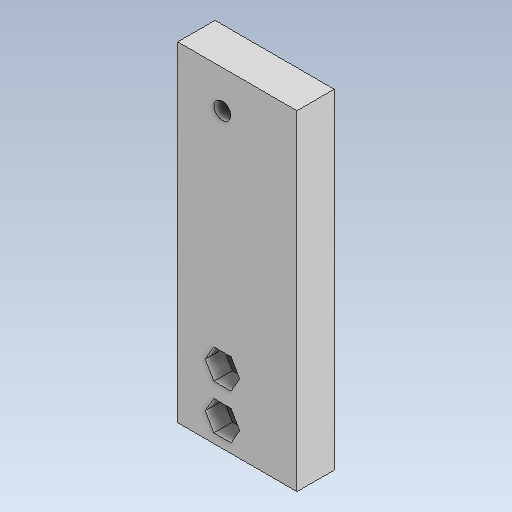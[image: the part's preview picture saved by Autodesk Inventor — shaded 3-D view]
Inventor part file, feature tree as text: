
AUTODESK INVENTOR PART (.ipt)
format: ipt  version: 2020 (Build 240168000, 168)  size: 152,576 bytes
history: native  units: mm
features: other x11, reference x8, sketch x5, extrude x3, projected_geometry x3, hole x2
ambient origin geometry x8: Origin, YZ Plane, XZ Plane, XY Plane, X Axis, Y Axis, Z Axis, Center Point
bodies: Body1 (feature_tree)
feature tree (32):
  other  "솔리드1"
  sketch  "스케치1"
  other  "작업 평면1"
  extrude  "돌출1"  Depth=10.0mm TaperAngle=0.0deg
  extrude  "돌출2"  Depth=8.0mm
  hole  "구멍1"  [1 undecoded]
  extrude  "돌출3"  Depth=5.0mm TaperAngle=0.0deg
  hole  "구멍2"  [1 undecoded]
  reference  "참조1"
  reference  "참조2"
  reference  "참조3"
  reference  "참조4"
  reference  "참조5"
  reference  "참조6"
  reference  "참조7"
  sketch  "스케치2"
  reference  "참조8"
  sketch  "스케치3"
  projected_geometry  "투영된 루프1"
  projected_geometry  "투영된 루프2"
  sketch  "스케치4"
  sketch  "스케치6"
  projected_geometry  "투영된 루프3"
  other  "<userpath>\Documents\Inventor\CoMoVi\Package\v5.iam"
  other  "v5.iam"
  other  "볼트 연결:27"
  other  "ISO 4762 M5 x 16:1"
  other  "볼트 연결:28"
  other  "Bumper_assey2:1"
  other  "bumper_final_3:1"
  other  "bumper_final_5:1"
  other  "Axel_arch_final_v4:1"
note: 2 required parameter values undecoded (feature->parameter linkage not recoverable at this tier; creation-order binding heuristic only, values carry confidence <= 0.55)
